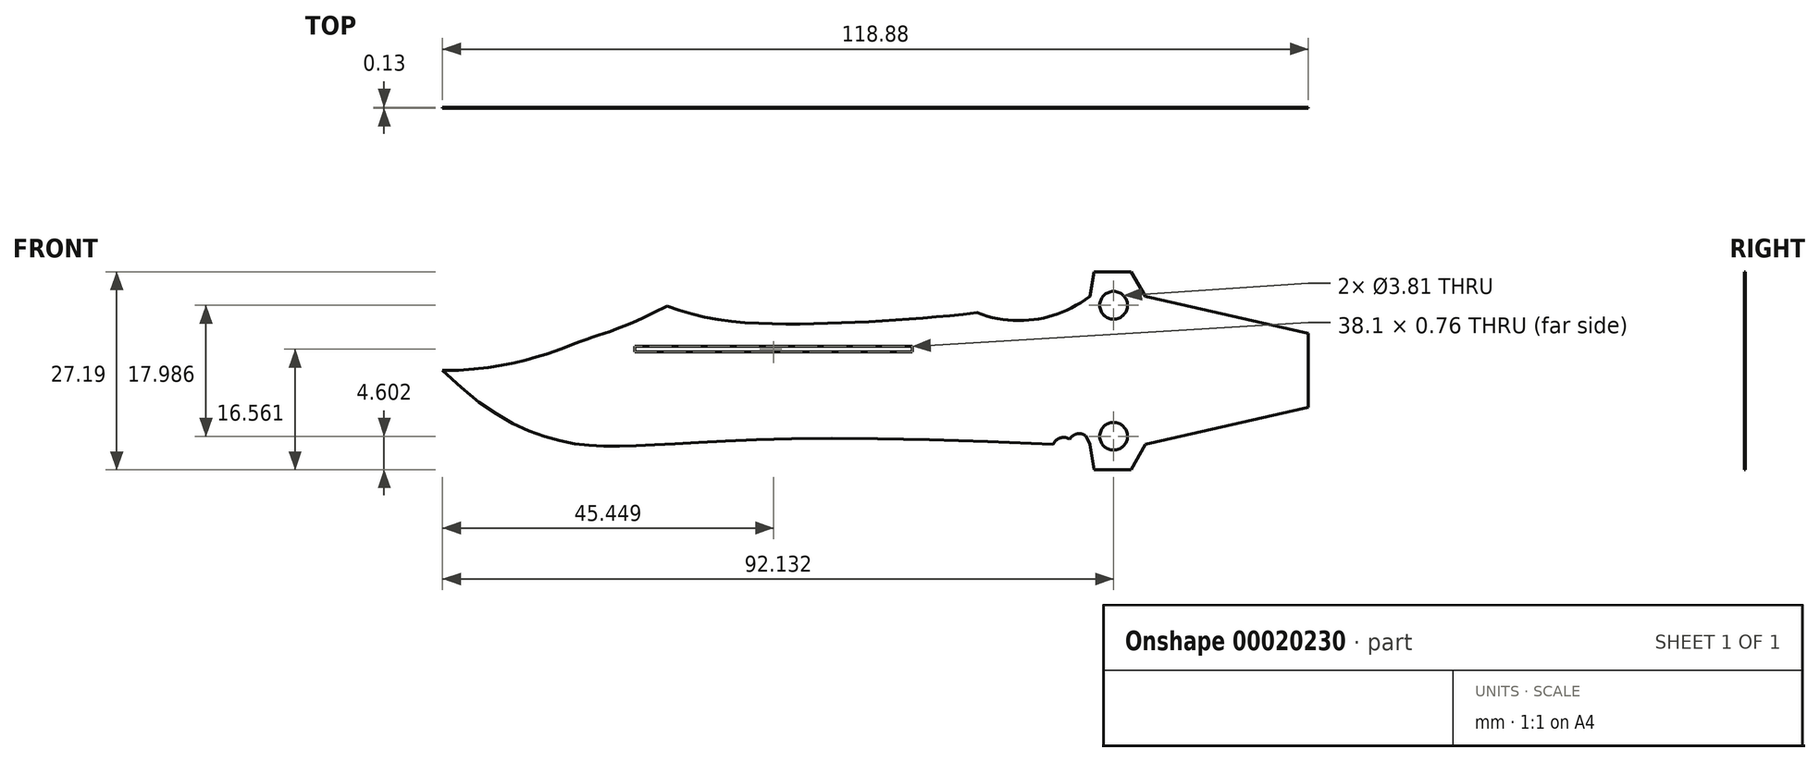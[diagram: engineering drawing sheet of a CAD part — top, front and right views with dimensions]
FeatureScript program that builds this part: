
annotation { "Feature Type Name" : "Feature", "Feature Type Description" : "" }
export const myFeature = defineFeature(function(context is Context, id is Id, definition is map)
    precondition{}
    {
        {
            var Q0;
            Q0=qCreatedBy(makeId("Front.planeOp"),FACE);
            var sketch = newSketch(context, id + "F0", { "sketchPlane" : qUnion([Q0])});
            skLineSegment(sketch, "E0", {"start": v(0, 0) * mm, "end": v(-88.9, 0) * mm});
            skLineSegment(sketch, "E1", {"start": v(-88.9, 0) * mm, "end": v(-69.14, 0) * mm});
            skFitSpline(sketch, "E2", {"points": [v(-88.9, 0) * mm, v(-69.14, 4.27) * mm, v(-58.05, 8.87) * mm], "startDerivative": vector(52.47, 0) * mm, "endDerivative": vector(45.4, 23.33) * mm});
            skLineSegment(sketch, "E3", {"start": v(-62.5, 0) * mm, "end": v(-62.5, 2.54) * mm});
            skLineSegment(sketch, "E4", {"start": v(-62.5, 2.54) * mm, "end": v(-24.4, 2.54) * mm});
            skLineSegment(sketch, "E5", {"start": v(-24.4, 2.54) * mm, "end": v(-24.4, 3.3) * mm});
            skLineSegment(sketch, "E6", {"start": v(-24.4, 3.3) * mm, "end": v(-62.5, 3.3) * mm});
            skLineSegment(sketch, "E7", {"start": v(-62.5, 3.3) * mm, "end": v(-62.5, 2.54) * mm});
            skFitSpline(sketch, "E8", {"points": [v(-88.9, 0) * mm, v(-69.98, -10.16) * mm, v(-5.08, -10.16) * mm], "startDerivative": vector(60.32, -58.87) * mm, "endDerivative": vector(218.63, -11.1) * mm});
            skArc(sketch, "E9", {"start": v(-2.79, -9.44) * mm, "mid": v(-4.1, -9.27) * mm, "end": v(-5.08, -10.16) * mm});
            skArc(sketch, "E10", {"start": v(0, -10.16) * mm, "mid": v(0, -10.12) * mm, "end": v(0, -10.09) * mm});
            skLineSegment(sketch, "E11", {"start": v(-62.5, 0) * mm, "end": v(-37.1, 0) * mm});
            skFitSpline(sketch, "E12", {"points": [v(-58.05, 8.87) * mm, v(-37.1, 6.45) * mm, v(-15.52, 7.93) * mm], "startDerivative": vector(37.84, -15.4) * mm, "endDerivative": vector(43.07, 4.92) * mm});
            skArc(sketch, "E13.trimOffspring", {"start": v(-0.62, -8.95) * mm, "mid": v(-1.81, -8.7) * mm, "end": v(-2.79, -9.44) * mm});
            skLineSegment(sketch, "E14", {"start": v(-0.62, -8.95) * mm, "end": v(0, -10.16) * mm});
            skFitSpline(sketch, "E15", {"points": [v(-15.52, 7.93) * mm, v(-7.33, 7.04) * mm, v(0, 10.16) * mm], "startDerivative": vector(15.8, -6.13) * mm, "endDerivative": vector(15.26, 10.41) * mm});
            skLineSegment(sketch, "E16", {"start": v(0.58, -13.64) * mm, "end": v(5.66, -13.64) * mm});
            skLineSegment(sketch, "E17", {"start": v(0.58, 13.55) * mm, "end": v(5.66, 13.55) * mm});
            skLineSegment(sketch, "E18", {"start": v(0, -10.16) * mm, "end": v(0.58, -13.64) * mm});
            skLineSegment(sketch, "E19", {"start": v(7.62, -10.16) * mm, "end": v(5.66, -13.64) * mm});
            skLineSegment(sketch, "E20", {"start": v(0.58, 13.55) * mm, "end": v(0, 10.16) * mm});
            skLineSegment(sketch, "E21", {"start": v(5.66, 13.55) * mm, "end": v(7.62, 10.16) * mm});
            skPoint(sketch, "E22.orphan", {"position": v(7.62, 13.55) * mm});
            skLineSegment(sketch, "E23", {"start": v(29.98, 5.08) * mm, "end": v(29.98, -5.08) * mm});
            skLineSegment(sketch, "E24", {"start": v(7.62, -10.16) * mm, "end": v(29.98, -5.08) * mm});
            skLineSegment(sketch, "E25", {"start": v(29.98, 5.08) * mm, "end": v(7.62, 10.16) * mm});
            skPoint(sketch, "E26.start.orphan", {"position": v(0, -5.08) * mm});
            skPoint(sketch, "E27.start.orphan", {"position": v(0, 5.08) * mm});
            skCircle(sketch, "E28", {"center": v(3.23, 8.95) * mm, "radius": 1.9 * mm});
            skCircle(sketch, "E29", {"center": v(3.23, -9.04) * mm, "radius": 1.9 * mm});
            skSolve(sketch);
        }
        {
            var Q0;
            Q0=makeQuery(id+"F0.imprint","IMPRINT",FACE,{"disambiguationData":[TD([[makeQuery(id+"F0.imprint","IMPRINT",EDGE,{"derivedFrom":sQuery(id+"F0.wireOp",EDGE,"E2")}),-1.0]])]});
            extrude(context, id + "F1", {"entities" : qUnion([Q0]), "depth" : 0.13 * mm});
        }
    });
